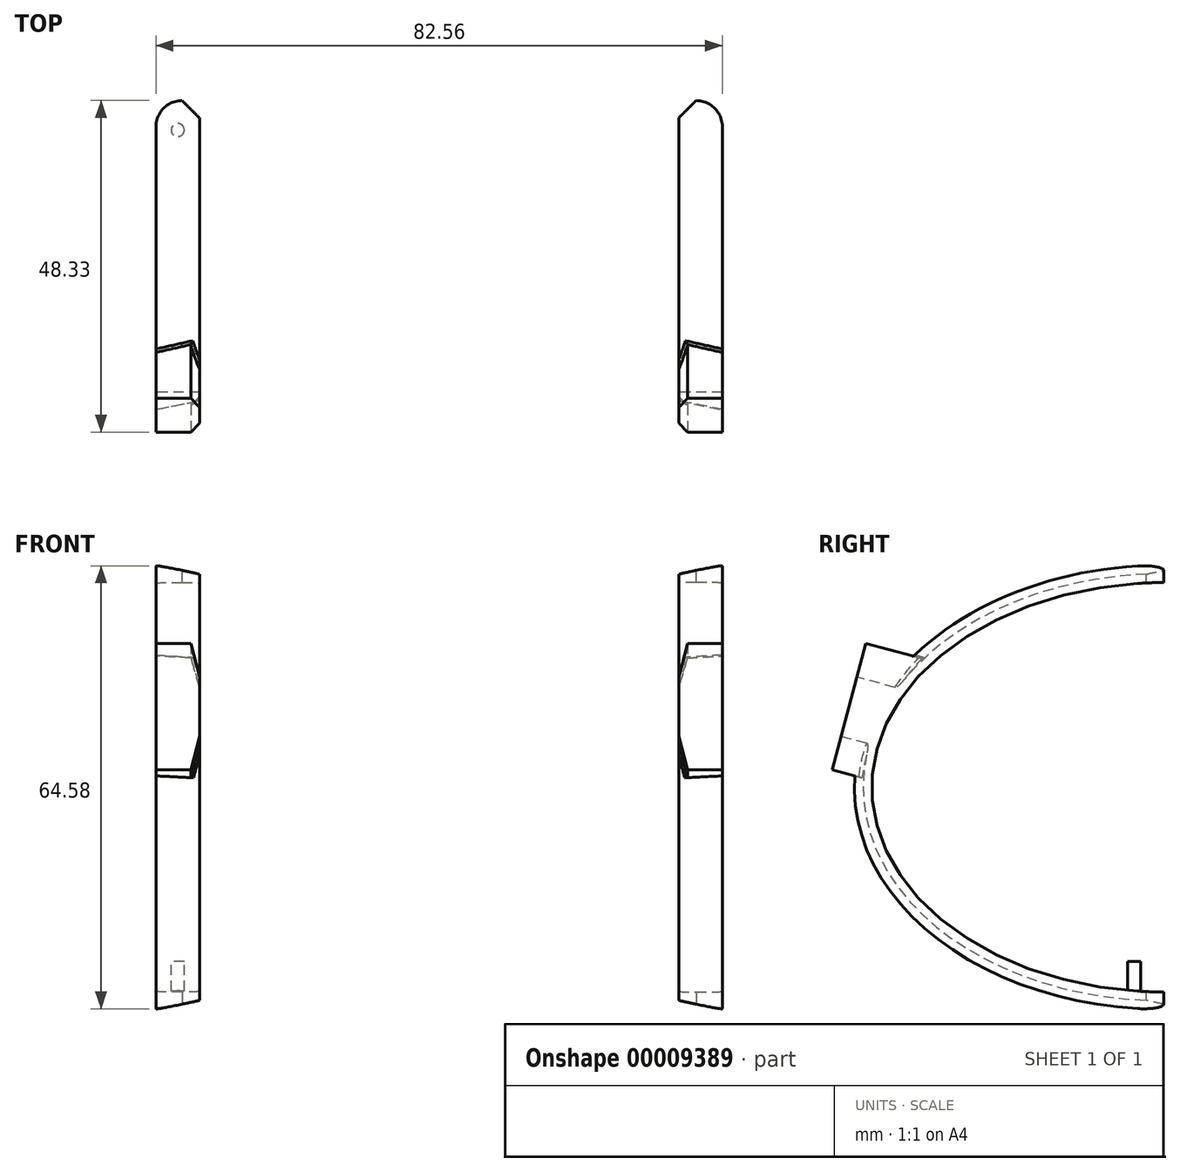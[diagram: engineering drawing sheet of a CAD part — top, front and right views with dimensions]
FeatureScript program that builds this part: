
annotation { "Feature Type Name" : "Feature", "Feature Type Description" : "" }
export const myFeature = defineFeature(function(context is Context, id is Id, definition is map)
    precondition{}
    {
        {
            var Q0;
            Q0=qCreatedBy(makeId("Front.planeOp"),FACE);
            var sketch = newSketch(context, id + "F0", { "sketchPlane" : qUnion([Q0])});
            skLineSegment(sketch, "E0.bottom", {"start": v(-3.17, 0.64) * mm, "end": v(3.18, -0.64) * mm});
            skLineSegment(sketch, "E0.top", {"start": v(-3.17, -1.9) * mm, "end": v(3.18, -1.9) * mm});
            skLineSegment(sketch, "E0.left", {"start": v(-3.17, 0.63) * mm, "end": v(-3.17, -1.9) * mm});
            skLineSegment(sketch, "E0.right", {"start": v(3.18, -0.64) * mm, "end": v(3.18, -1.9) * mm});
            skSolve(sketch);
        }
        {
            var Q0;
            Q0=qCreatedBy(makeId("Right.planeOp"),FACE);
            var sketch = newSketch(context, id + "F1", { "sketchPlane" : qUnion([Q0])});
            skEllipticalArc(sketch, "E1", {});
            const initialGuessF1  = {"E1": [0, -0.03175, 0, -1, 0.03175, 0.04445, 3.141592653589793, 6.283185307179586]};
            skSetInitialGuess(sketch, initialGuessF1);
            skSolve(sketch);
        }
        {
            var Q0;
            Q0 = qSketchRegion(id + "F0", true);
            var Q1;
            Q1 = qBodyType(qCreatedBy(id + "F1" ,EDGE), BodyType.WIRE);
            sweep(context, id + "F2", {"profiles" : qUnion([Q0]), "path" : qUnion([Q1])});
        }
        {
            var Q0;
            Q0=qCreatedBy(makeId("Front.planeOp"),FACE);
            cPlane(context, id + "F3", {"entities" : qUnion([Q0]), "cplaneType" : CPlaneType.OFFSET, "offset" : 44.45 * mm, "width" : 152.4 * mm, "height" : 152.4 * mm});
        }
        {
            var Q0;
            Q0=qCreatedBy(id+"F3.planeOp",FACE);
            var sketch = newSketch(context, id + "F4", { "sketchPlane" : qUnion([Q0])});
            skLineSegment(sketch, "E2", {"start": v(-56.46, 0) * mm, "end": v(56.46, 0) * mm});
            skPoint(sketch, "E3", {"position": v(0, 0) * mm});
            skSolve(sketch);
        }
        {
            var Q0;
            Q0=sQuery(id+"F4.wireOp",EDGE,"E2");
            cPlane(context, id + "F5", {"entities" : qUnion([Q0]), "cplaneType" : CPlaneType.LINE_ANGLE, "offset" : 152.4 * mm, "angle" : 165 * degree, "width" : 152.4 * mm, "height" : 152.4 * mm});
        }
        {
            var Q0;
            Q0=qCreatedBy(id+"F5.planeOp",FACE);
            cPlane(context, id + "F6", {"entities" : qUnion([Q0]), "cplaneType" : CPlaneType.OFFSET, "offset" : 3.8 * mm, "oppositeDirection" : true, "width" : 152.4 * mm, "height" : 152.4 * mm});
        }
        {
            var Q0;
            Q0=qCreatedBy(id+"F5.planeOp",FACE);
            var sketch = newSketch(context, id + "F7", { "sketchPlane" : qUnion([Q0])});
            skLineSegment(sketch, "E4.bottom", {"start": v(3.17, -40.71) * mm, "end": v(-3.18, -40.71) * mm});
            skLineSegment(sketch, "E4.top", {"start": v(3.17, -21.66) * mm, "end": v(-3.17, -21.66) * mm});
            skLineSegment(sketch, "E4.left", {"start": v(3.17, -40.71) * mm, "end": v(3.17, -21.66) * mm});
            skLineSegment(sketch, "E4.right", {"start": v(-3.17, -40.71) * mm, "end": v(-3.17, -21.66) * mm});
            skSolve(sketch);
        }
        {
            var Q0;
            Q0=makeQuery(id+"F7.imprint","IMPRINT",FACE,{"disambiguationData":[TD([[makeQuery(id+"F7.imprint","IMPRINT",EDGE,{"derivedFrom":sQuery(id+"F7.wireOp",EDGE,"E4.bottom")}),-1.0]])]});
            var Q1;
            Q1=makeQuery(id+"F2.opSweep","SWEPT_FACE",FACE,{"disambiguationData":[OSD([sQuery(id+"F0.wireOp",EDGE,"E0.bottom"),sQuery(id+"F1.wireOp",EDGE,"E1")])]});
            extrude(context, id + "F8", {"entities" : qUnion([Q0]), "operationType" : NewBodyOperationType.ADD, "endBound" : BoundingType.UP_TO_SURFACE, "oppositeDirection" : true, "endBoundEntityFace" : qUnion([Q1]), "depth" : 25.4 * mm});
        }
        {
            var Q0;
            Q0=qCreatedBy(id+"F6.planeOp",FACE);
            var sketch = newSketch(context, id + "F9", { "sketchPlane" : qUnion([Q0])});
            skLineSegment(sketch, "E5.bottom", {"start": v(6.5, -44.2) * mm, "end": v(-25.07, -44.2) * mm});
            skLineSegment(sketch, "E5.top", {"start": v(6.5, -12.83) * mm, "end": v(-25.07, -12.83) * mm});
            skLineSegment(sketch, "E5.left", {"start": v(6.5, -44.2) * mm, "end": v(6.5, -12.83) * mm});
            skLineSegment(sketch, "E5.right", {"start": v(-25.07, -44.2) * mm, "end": v(-25.07, -12.83) * mm});
            skSolve(sketch);
        }
        {
            var Q0;
            Q0 = qSketchRegion(id + "F9", true);
            var Q1;
            Q1=makeQuery(id+"F8.opExtrude","CAP_FACE",FACE,{"disambiguationData":[OSD([sQuery(id+"F7.wireOp",EDGE,"E4.bottom"),sQuery(id+"F7.wireOp",EDGE,"E4.top"),sQuery(id+"F7.wireOp",EDGE,"E4.left"),sQuery(id+"F7.wireOp",EDGE,"E4.right")])],"isStart":true});
            extrude(context, id + "F10", {"entities" : qUnion([Q0]), "operationType" : NewBodyOperationType.REMOVE, "endBound" : BoundingType.UP_TO_SURFACE, "endBoundEntityFace" : qUnion([Q1]), "depth" : 25.4 * mm});
        }
        {
            var Q0;
            Q0=makeQuery(id+"F8.opExtrude","SWEPT_EDGE",EDGE,{"disambiguationData":[OSD([sQuery(id+"F7.wireOp",EDGE,"E4.top"),sQuery(id+"F7.wireOp",EDGE,"E4.left")])]});
            var Q1;
            Q1=makeQuery(id+"F8.opExtrude","SWEPT_EDGE",EDGE,{"disambiguationData":[OSD([sQuery(id+"F7.wireOp",EDGE,"E4.bottom"),sQuery(id+"F7.wireOp",EDGE,"E4.left")])]});
            chamfer(context, id + "F11", {"entities" : qUnion([Q0, Q1]), "chamferType" : ChamferType.TWO_OFFSETS, "width1" : 5.08 * mm, "oppositeDirection" : false, "width2" : 1.27 * mm, "tangentPropagation" : true});
        }
        {
            var Q0;
            {var subQ0=sQuery(id+"F1.wireOp",EDGE,"E1");var subQ2=sQuery(id+"F7.wireOp",EDGE,"E4.top");var subQ4=sQuery(id+"F0.wireOp",EDGE,"E0.bottom");var subQ5=sQuery(id+"F7.wireOp",EDGE,"E4.left");Q0=makeQuery(id+"F11.opChamfer","BLEND_EDGE",EDGE,{"blendedFrom":[makeQuery(id+"F8.opExtrude","SWEPT_EDGE",EDGE,{"disambiguationData":[OSD([subQ2,subQ5])]}),makeQuery(id+"F8.boolean.opBoolean","SPLIT",FACE,{"disambiguationData":[TD([makeQuery(id+"F8.opExtrude","SWEPT_FACE",FACE,{"disambiguationData":[OSD([subQ2])]})])],"derivedFrom":makeQuery(id+"F2.opSweep","SWEPT_FACE",FACE,{"disambiguationData":[OSD([subQ4,subQ0])]})})],"blendedInto":[makeQuery(id+"F8.boolean.opBoolean","SPLIT",FACE,{"disambiguationData":[TD([makeQuery(id+"F8.opExtrude","SWEPT_FACE",FACE,{"disambiguationData":[OSD([subQ2])]})])],"derivedFrom":makeQuery(id+"F2.opSweep","SWEPT_FACE",FACE,{"disambiguationData":[OSD([subQ4,subQ0])]})})]});}
            var Q1;
            Q1=makeQuery(id+"F8.opExtrude","CAP_EDGE",EDGE,{"disambiguationData":[OSD([sQuery(id+"F7.wireOp",EDGE,"E4.top")])],"isStart":false});
            var Q2;
            {var subQ0=sQuery(id+"F7.wireOp",EDGE,"E4.bottom");var subQ1=sQuery(id+"F1.wireOp",EDGE,"E1");var subQ4=sQuery(id+"F0.wireOp",EDGE,"E0.bottom");var subQ5=sQuery(id+"F7.wireOp",EDGE,"E4.left");Q2=makeQuery(id+"F11.opChamfer","BLEND_EDGE",EDGE,{"blendedFrom":[makeQuery(id+"F8.opExtrude","SWEPT_EDGE",EDGE,{"disambiguationData":[OSD([subQ0,subQ5])]}),makeQuery(id+"F8.boolean.opBoolean","SPLIT",FACE,{"disambiguationData":[TD([makeQuery(id+"F8.opExtrude","SWEPT_FACE",FACE,{"disambiguationData":[OSD([subQ0])]})])],"derivedFrom":makeQuery(id+"F2.opSweep","SWEPT_FACE",FACE,{"disambiguationData":[OSD([subQ4,subQ1])]})})],"blendedInto":[makeQuery(id+"F8.boolean.opBoolean","SPLIT",FACE,{"disambiguationData":[TD([makeQuery(id+"F8.opExtrude","SWEPT_FACE",FACE,{"disambiguationData":[OSD([subQ0])]})])],"derivedFrom":makeQuery(id+"F2.opSweep","SWEPT_FACE",FACE,{"disambiguationData":[OSD([subQ4,subQ1])]})})]});}
            var Q3;
            Q3=makeQuery(id+"F8.opExtrude","CAP_EDGE",EDGE,{"disambiguationData":[OSD([sQuery(id+"F7.wireOp",EDGE,"E4.bottom")])],"isStart":false});
            fillet(context, id + "F12", {"entities" : qUnion([Q0, Q1, Q2, Q3]), "radius" : 0.5 * mm, "tangentPropagation" : true, "allowEdgeOverflow" : false});
        }
        {
            var Q0;
            Q0=makeQuery(id+"F2.opSweep","CAP_EDGE",EDGE,{"disambiguationData":[OSD([sQuery(id+"F0.wireOp",EDGE,"E0.left"),sQuery(id+"F1.wireOp",VERTEX,"E1.start")])],"isStart":true});
            var Q1;
            Q1=makeQuery(id+"F2.opSweep","CAP_EDGE",EDGE,{"disambiguationData":[OSD([sQuery(id+"F0.wireOp",EDGE,"E0.left"),sQuery(id+"F1.wireOp",VERTEX,"E1.end")])],"isStart":false});
            fillet(context, id + "F13", {"entities" : qUnion([Q0, Q1]), "radius" : 3.8 * mm, "tangentPropagation" : true, "allowEdgeOverflow" : false});
        }
        {
            var Q0;
            Q0=makeQuery(id+"F2.opSweep","CAP_EDGE",EDGE,{"disambiguationData":[OSD([sQuery(id+"F0.wireOp",EDGE,"E0.right"),sQuery(id+"F1.wireOp",VERTEX,"E1.start")])],"isStart":true});
            var Q1;
            Q1=makeQuery(id+"F2.opSweep","CAP_EDGE",EDGE,{"disambiguationData":[OSD([sQuery(id+"F0.wireOp",EDGE,"E0.right"),sQuery(id+"F1.wireOp",VERTEX,"E1.end")])],"isStart":false});
            chamfer(context, id + "F14", {"entities" : qUnion([Q0, Q1]), "width" : 2.54 * mm, "tangentPropagation" : true});
        }
        {
            var Q0;
            Q0=qCreatedBy(makeId("Top.planeOp"),FACE);
            cPlane(context, id + "F15", {"entities" : qUnion([Q0]), "cplaneType" : CPlaneType.OFFSET, "offset" : 57.15 * mm, "oppositeDirection" : true, "width" : 152.4 * mm, "height" : 152.4 * mm});
        }
        {
            var Q0;
            Q0=qCreatedBy(id+"F15.planeOp",FACE);
            var sketch = newSketch(context, id + "F16", { "sketchPlane" : qUnion([Q0])});
            skCircle(sketch, "E6", {"center": v(0, -4.3) * mm, "radius": 0.95 * mm});
            skSolve(sketch);
        }
        {
            var Q0;
            Q0=makeQuery(id+"F16.imprint","IMPRINT",FACE,{"disambiguationData":[TD([[makeQuery(id+"F16.imprint","IMPRINT",EDGE,{"derivedFrom":sQuery(id+"F16.wireOp",EDGE,"E6")}),1.0]])]});
            extrude(context, id + "F17", {"entities" : qUnion([Q0]), "endBound" : BoundingType.UP_TO_NEXT, "oppositeDirection" : true, "depth" : 25.4 * mm});
        }
        {
            var Q0;
            Q0=qCreatedBy(makeId("Right.planeOp"),FACE);
            cPlane(context, id + "F18", {"entities" : qUnion([Q0]), "cplaneType" : CPlaneType.OFFSET, "offset" : 38.1 * mm, "width" : 152.4 * mm, "height" : 152.4 * mm});
        }
        {
            var Q0;
            Q0=makeQuery(id+"F2.opSweep","SWEPT_BODY",BODY,{"disambiguationData":[OSD([sQuery(id+"F0.wireOp",EDGE,"E0.bottom"),sQuery(id+"F0.wireOp",EDGE,"E0.top"),sQuery(id+"F0.wireOp",EDGE,"E0.left"),sQuery(id+"F0.wireOp",EDGE,"E0.right"),sQuery(id+"F1.wireOp",EDGE,"E1")])]});
            var Q1;
            Q1=qCreatedBy(id+"F18.planeOp",FACE);
            mirror(context, id + "F19", {"entities" : qUnion([Q0]), "mirrorPlane" : qUnion([Q1])});
        }
    });
